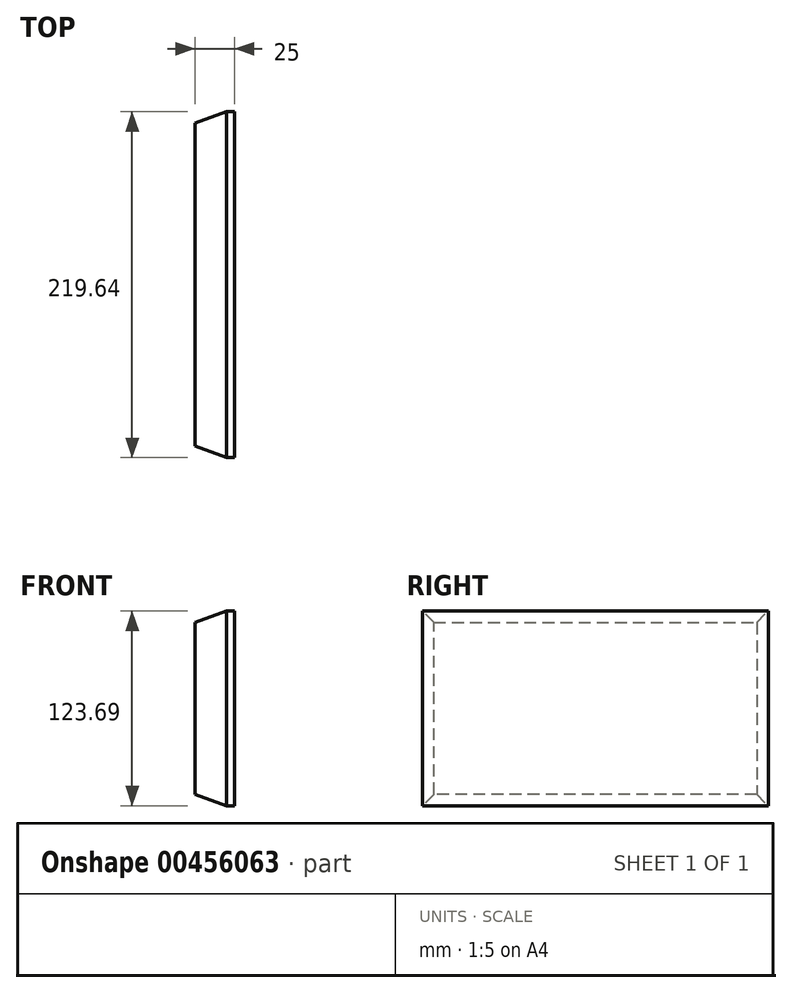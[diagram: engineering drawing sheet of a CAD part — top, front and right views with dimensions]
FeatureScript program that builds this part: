
annotation { "Feature Type Name" : "Feature", "Feature Type Description" : "" }
export const myFeature = defineFeature(function(context is Context, id is Id, definition is map)
    precondition{}
    {
        {
            var Q0;
            Q0=qCreatedBy(makeId("Right.planeOp"),FACE);
            var sketch = newSketch(context, id + "F0", { "sketchPlane" : qUnion([Q0])});
            skLineSegment(sketch, "E0.bottom", {"start": v(165.34, 116.35) * mm, "end": v(-54.3, 116.35) * mm});
            skLineSegment(sketch, "E0.top", {"start": v(165.34, -7.34) * mm, "end": v(-54.3, -7.34) * mm});
            skLineSegment(sketch, "E0.left", {"start": v(165.34, 116.35) * mm, "end": v(165.34, -7.34) * mm});
            skLineSegment(sketch, "E0.right", {"start": v(-54.3, 116.35) * mm, "end": v(-54.3, -7.34) * mm});
            skSolve(sketch);
        }
        {
            var Q0;
            Q0=makeQuery(id+"F0.imprint","IMPRINT",FACE,{"disambiguationData":[TD([[makeQuery(id+"F0.imprint","IMPRINT",EDGE,{"derivedFrom":sQuery(id+"F0.wireOp",EDGE,"E0.bottom")}),1.0]])]});
            extrude(context, id + "F1", {"entities" : qUnion([Q0]), "depth" : 25 * mm});
        }
        {
            var Q0;
            Q0=makeQuery(id+"F1.opExtrude","CAP_FACE",FACE,{"disambiguationData":[OSD([sQuery(id+"F0.wireOp",EDGE,"E0.bottom"),sQuery(id+"F0.wireOp",EDGE,"E0.top"),sQuery(id+"F0.wireOp",EDGE,"E0.left"),sQuery(id+"F0.wireOp",EDGE,"E0.right")])],"isStart":true});
            chamfer(context, id + "F2", {"entities" : qUnion([Q0]), "chamferType" : ChamferType.OFFSET_ANGLE, "width" : 20 * mm, "oppositeDirection" : false, "angle" : 20 * degree, "tangentPropagation" : true});
        }
    });
